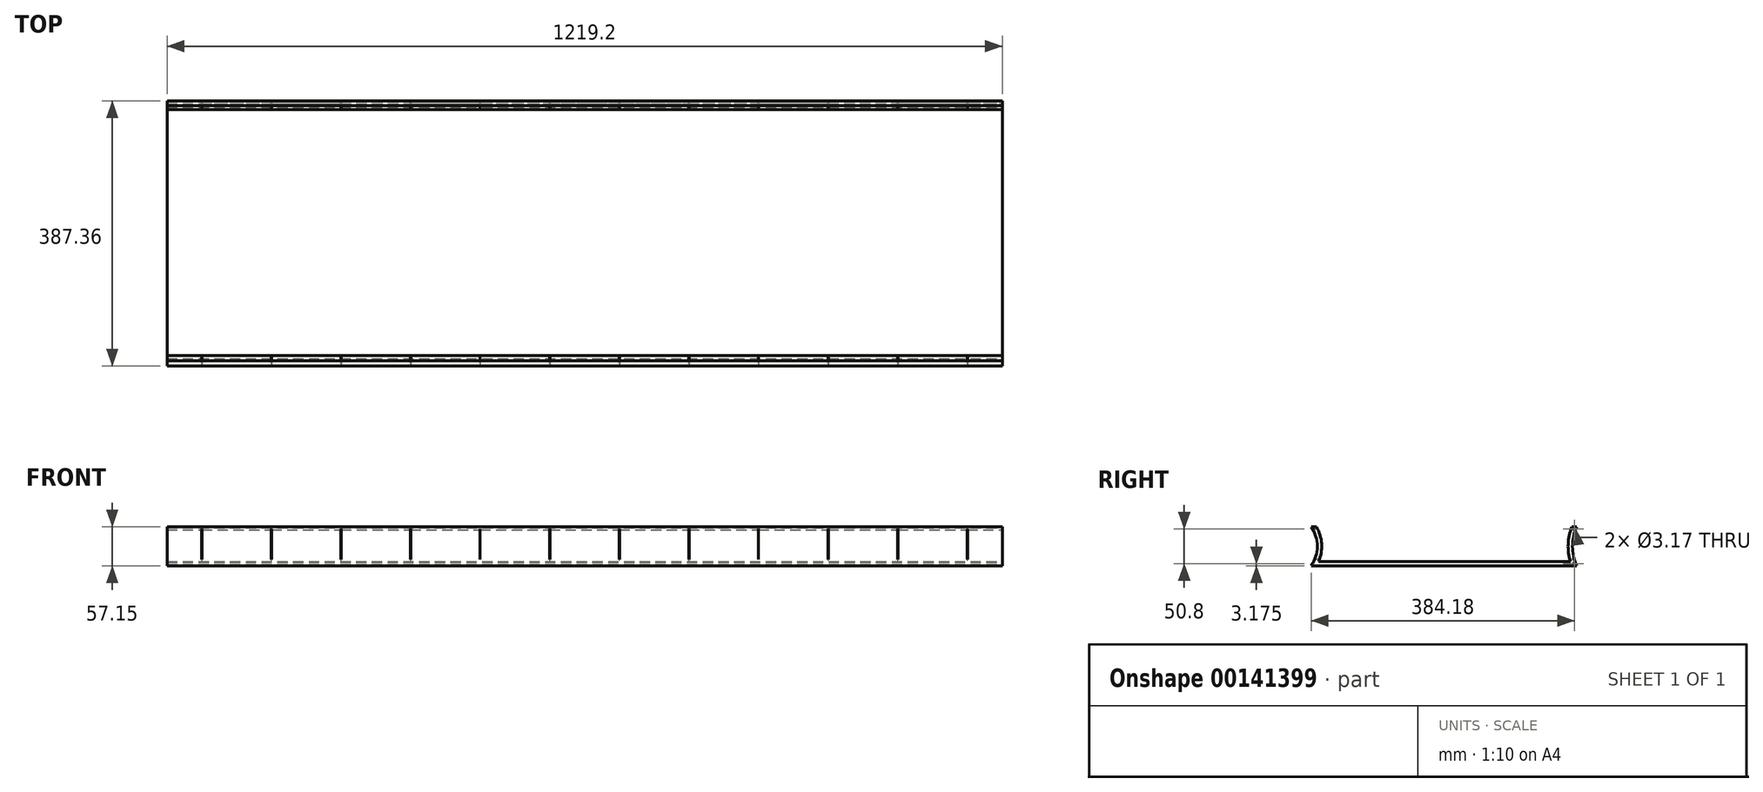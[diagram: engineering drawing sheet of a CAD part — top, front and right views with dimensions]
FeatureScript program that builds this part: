
annotation { "Feature Type Name" : "Feature", "Feature Type Description" : "" }
export const myFeature = defineFeature(function(context is Context, id is Id, definition is map)
    precondition{}
    {
        {
            var Q0;
            Q0=qCreatedBy(makeId("Right.planeOp"),FACE);
            var sketch = newSketch(context, id + "F0", { "sketchPlane" : qUnion([Q0])});
            skLineSegment(sketch, "E0", {"start": v(-193.68, 0) * mm, "end": v(193.68, 0) * mm});
            skArc(sketch, "E1", {"start": v(193.67, 57.15) * mm, "mid": v(187.56, 28.57) * mm, "end": v(193.68, 0) * mm});
            skArc(sketch, "E2", {"start": v(186.77, 57.15) * mm, "mid": v(181.29, 31.94) * mm, "end": v(184.53, 6.35) * mm});
            skLineSegment(sketch, "E3", {"start": v(184.53, 6.35) * mm, "end": v(-183.02, 6.35) * mm});
            skArc(sketch, "E4", {"start": v(-183.02, 6.35) * mm, "mid": v(-178.64, 32.12) * mm, "end": v(-186.18, 57.15) * mm});
            skArc(sketch, "E5", {"start": v(-193.68, 0) * mm, "mid": v(-184.88, 28.57) * mm, "end": v(-193.68, 57.15) * mm});
            skLineSegment(sketch, "E6", {"start": v(-193.68, 57.15) * mm, "end": v(-186.18, 57.15) * mm});
            skLineSegment(sketch, "E7", {"start": v(186.77, 57.15) * mm, "end": v(193.68, 57.15) * mm});
            skSolve(sketch);
        }
        {
            var Q0;
            Q0 = qSketchRegion(id + "F0", true);
            extrude(context, id + "F1", {"entities" : qUnion([Q0]), "oppositeDirection" : true, "depth" : 1219.2 * mm});
        }
        {
            var Q0;
            Q0=makeQuery(id+"F1.opExtrude","CAP_FACE",FACE,{"disambiguationData":[OSD([sQuery(id+"F0.wireOp",EDGE,"E0"),sQuery(id+"F0.wireOp",EDGE,"E1"),sQuery(id+"F0.wireOp",EDGE,"E2"),sQuery(id+"F0.wireOp",EDGE,"E3"),sQuery(id+"F0.wireOp",EDGE,"E4"),sQuery(id+"F0.wireOp",EDGE,"E5"),sQuery(id+"F0.wireOp",EDGE,"E6"),sQuery(id+"F0.wireOp",EDGE,"E7")])],"isStart":true});
            var sketch = newSketch(context, id + "F2", { "sketchPlane" : qUnion([Q0])});
            skCircle(sketch, "E8", {"center": v(190.5, 53.97) * mm, "radius": 1.59 * mm});
            skCircle(sketch, "E9", {"center": v(190.5, 3.17) * mm, "radius": 1.59 * mm});
            skSolve(sketch);
        }
        {
            var Q0;
            Q0 = qSketchRegion(id + "F2", true);
            extrude(context, id + "F3", {"entities" : qUnion([Q0]), "operationType" : NewBodyOperationType.REMOVE, "endBound" : BoundingType.THROUGH_ALL, "oppositeDirection" : true, "depth" : 25.4 * mm});
        }
        {
            var Q0;
            Q0=qCreatedBy(makeId("Front.planeOp"),FACE);
            var sketch = newSketch(context, id + "F4", { "sketchPlane" : qUnion([Q0])});
            skLineSegment(sketch, "E10.bottom", {"start": v(-50.8, 9.52) * mm, "end": v(-51.12, 9.52) * mm});
            skLineSegment(sketch, "E10.top", {"start": v(-50.8, 53.97) * mm, "end": v(-51.12, 53.97) * mm});
            skLineSegment(sketch, "E10.left", {"start": v(-50.8, 9.52) * mm, "end": v(-50.8, 53.97) * mm});
            skLineSegment(sketch, "E10.right", {"start": v(-51.12, 9.52) * mm, "end": v(-51.12, 53.97) * mm});
            skLineSegment(sketch, "E11.1.0.0", {"start": v(-152.4, 9.52) * mm, "end": v(-152.72, 9.52) * mm});
            skLineSegment(sketch, "E11.1.0.1", {"start": v(-152.72, 9.52) * mm, "end": v(-152.72, 53.97) * mm});
            skLineSegment(sketch, "E11.1.0.2", {"start": v(-152.4, 9.52) * mm, "end": v(-152.4, 53.97) * mm});
            skLineSegment(sketch, "E11.1.0.3", {"start": v(-152.4, 53.97) * mm, "end": v(-152.72, 53.97) * mm});
            skLineSegment(sketch, "E11.2.0.0", {"start": v(-254, 9.52) * mm, "end": v(-254.32, 9.52) * mm});
            skLineSegment(sketch, "E11.2.0.1", {"start": v(-254.32, 9.52) * mm, "end": v(-254.32, 53.97) * mm});
            skLineSegment(sketch, "E11.2.0.2", {"start": v(-254, 9.52) * mm, "end": v(-254, 53.97) * mm});
            skLineSegment(sketch, "E11.2.0.3", {"start": v(-254, 53.97) * mm, "end": v(-254.32, 53.97) * mm});
            skLineSegment(sketch, "E11.3.0.0", {"start": v(-355.6, 9.52) * mm, "end": v(-355.92, 9.52) * mm});
            skLineSegment(sketch, "E11.3.0.1", {"start": v(-355.92, 9.52) * mm, "end": v(-355.92, 53.97) * mm});
            skLineSegment(sketch, "E11.3.0.2", {"start": v(-355.6, 9.52) * mm, "end": v(-355.6, 53.97) * mm});
            skLineSegment(sketch, "E11.3.0.3", {"start": v(-355.6, 53.97) * mm, "end": v(-355.92, 53.97) * mm});
            skLineSegment(sketch, "E11.4.0.0", {"start": v(-457.2, 9.52) * mm, "end": v(-457.52, 9.52) * mm});
            skLineSegment(sketch, "E11.4.0.1", {"start": v(-457.52, 9.52) * mm, "end": v(-457.52, 53.97) * mm});
            skLineSegment(sketch, "E11.4.0.2", {"start": v(-457.2, 9.52) * mm, "end": v(-457.2, 53.97) * mm});
            skLineSegment(sketch, "E11.4.0.3", {"start": v(-457.2, 53.97) * mm, "end": v(-457.52, 53.97) * mm});
            skLineSegment(sketch, "E11.5.0.0", {"start": v(-558.8, 9.52) * mm, "end": v(-559.12, 9.52) * mm});
            skLineSegment(sketch, "E11.5.0.1", {"start": v(-559.12, 9.52) * mm, "end": v(-559.12, 53.97) * mm});
            skLineSegment(sketch, "E11.5.0.2", {"start": v(-558.8, 9.52) * mm, "end": v(-558.8, 53.97) * mm});
            skLineSegment(sketch, "E11.5.0.3", {"start": v(-558.8, 53.97) * mm, "end": v(-559.12, 53.97) * mm});
            skLineSegment(sketch, "E11.6.0.0", {"start": v(-660.4, 9.52) * mm, "end": v(-660.72, 9.52) * mm});
            skLineSegment(sketch, "E11.6.0.1", {"start": v(-660.72, 9.52) * mm, "end": v(-660.72, 53.97) * mm});
            skLineSegment(sketch, "E11.6.0.2", {"start": v(-660.4, 9.52) * mm, "end": v(-660.4, 53.97) * mm});
            skLineSegment(sketch, "E11.6.0.3", {"start": v(-660.4, 53.97) * mm, "end": v(-660.72, 53.97) * mm});
            skLineSegment(sketch, "E11.7.0.0", {"start": v(-762, 9.52) * mm, "end": v(-762.32, 9.52) * mm});
            skLineSegment(sketch, "E11.7.0.1", {"start": v(-762.32, 9.52) * mm, "end": v(-762.32, 53.97) * mm});
            skLineSegment(sketch, "E11.7.0.2", {"start": v(-762, 9.52) * mm, "end": v(-762, 53.97) * mm});
            skLineSegment(sketch, "E11.7.0.3", {"start": v(-762, 53.97) * mm, "end": v(-762.32, 53.97) * mm});
            skLineSegment(sketch, "E11.8.0.0", {"start": v(-863.6, 9.52) * mm, "end": v(-863.92, 9.52) * mm});
            skLineSegment(sketch, "E11.8.0.1", {"start": v(-863.92, 9.52) * mm, "end": v(-863.92, 53.97) * mm});
            skLineSegment(sketch, "E11.8.0.2", {"start": v(-863.6, 9.52) * mm, "end": v(-863.6, 53.97) * mm});
            skLineSegment(sketch, "E11.8.0.3", {"start": v(-863.6, 53.97) * mm, "end": v(-863.92, 53.97) * mm});
            skLineSegment(sketch, "E11.9.0.0", {"start": v(-965.2, 9.52) * mm, "end": v(-965.52, 9.52) * mm});
            skLineSegment(sketch, "E11.9.0.1", {"start": v(-965.52, 9.52) * mm, "end": v(-965.52, 53.97) * mm});
            skLineSegment(sketch, "E11.9.0.2", {"start": v(-965.2, 9.52) * mm, "end": v(-965.2, 53.97) * mm});
            skLineSegment(sketch, "E11.9.0.3", {"start": v(-965.2, 53.97) * mm, "end": v(-965.52, 53.97) * mm});
            skLineSegment(sketch, "E11.10.0.0", {"start": v(-1066.8, 9.52) * mm, "end": v(-1067.12, 9.52) * mm});
            skLineSegment(sketch, "E11.10.0.1", {"start": v(-1067.12, 9.52) * mm, "end": v(-1067.12, 53.97) * mm});
            skLineSegment(sketch, "E11.10.0.2", {"start": v(-1066.8, 9.52) * mm, "end": v(-1066.8, 53.97) * mm});
            skLineSegment(sketch, "E11.10.0.3", {"start": v(-1066.8, 53.97) * mm, "end": v(-1067.12, 53.97) * mm});
            skLineSegment(sketch, "E11.11.0.0", {"start": v(-1168.4, 9.52) * mm, "end": v(-1168.72, 9.52) * mm});
            skLineSegment(sketch, "E11.11.0.1", {"start": v(-1168.72, 9.52) * mm, "end": v(-1168.72, 53.97) * mm});
            skLineSegment(sketch, "E11.11.0.2", {"start": v(-1168.4, 9.52) * mm, "end": v(-1168.4, 53.97) * mm});
            skLineSegment(sketch, "E11.11.0.3", {"start": v(-1168.4, 53.97) * mm, "end": v(-1168.72, 53.97) * mm});
            skLineSegment(sketch, "E11.direction1", {"start": v(-51.12, 9.52) * mm, "end": v(-152.72, 9.52) * mm, "construction": true});
            skSolve(sketch);
        }
        {
            var Q0;
            Q0 = qSketchRegion(id + "F4", true);
            var Q1;
            Q1=makeQuery(id+"F1.opExtrude","SWEPT_FACE",FACE,{"disambiguationData":[OSD([sQuery(id+"F0.wireOp",EDGE,"E1")])]});
            var Q2;
            Q2=makeQuery(id+"F1.opExtrude","SWEPT_FACE",FACE,{"disambiguationData":[OSD([sQuery(id+"F0.wireOp",EDGE,"E5")])]});
            extrude(context, id + "F5", {"entities" : qUnion([Q0]), "operationType" : NewBodyOperationType.REMOVE, "endBound" : BoundingType.UP_TO_SURFACE, "oppositeDirection" : true, "endBoundEntityFace" : qUnion([Q1]), "depth" : 25.4 * mm, "hasSecondDirection" : true, "secondDirectionBound" : BoundingType.UP_TO_SURFACE, "secondDirectionOppositeDirection" : false, "secondDirectionBoundEntityFace" : qUnion([Q2]), "secondDirectionDepth" : 25.4 * mm});
        }
    });
